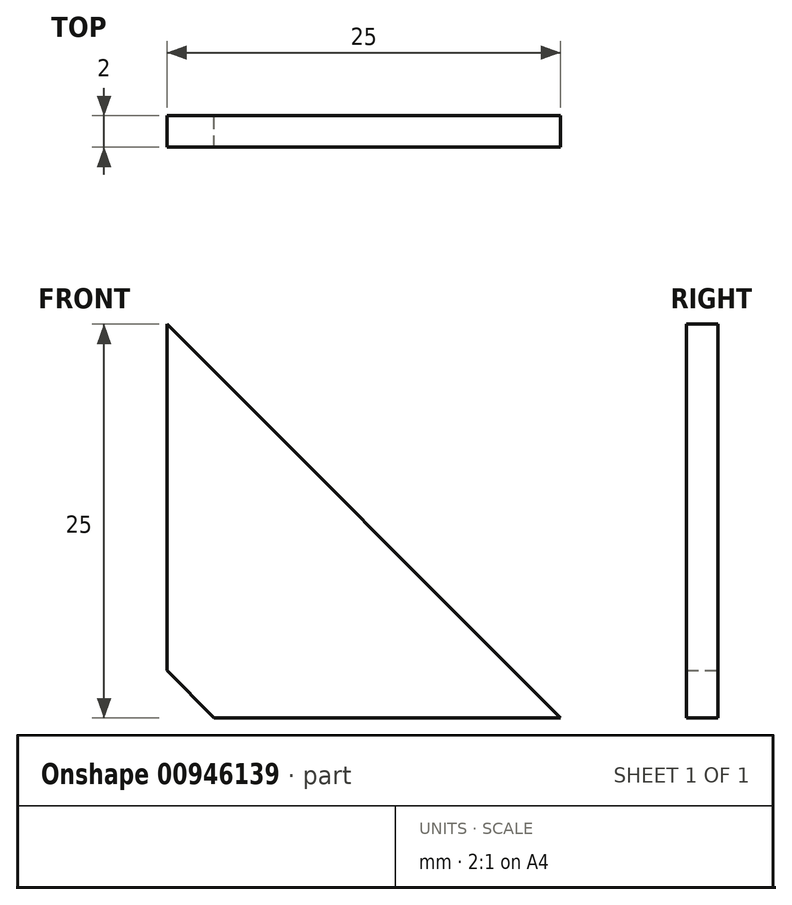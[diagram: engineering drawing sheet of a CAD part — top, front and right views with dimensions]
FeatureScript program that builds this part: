
annotation { "Feature Type Name" : "Feature", "Feature Type Description" : "" }
export const myFeature = defineFeature(function(context is Context, id is Id, definition is map)
    precondition{}
    {
        {
            var Q0;
            Q0=qCreatedBy(makeId("Front.planeOp"),FACE);
            var sketch = newSketch(context, id + "F0", { "sketchPlane" : qUnion([Q0])});
            skLineSegment(sketch, "E0", {"start": v(0, 0) * mm, "end": v(0, 25) * mm});
            skLineSegment(sketch, "E1", {"start": v(0, 25) * mm, "end": v(25, 0) * mm});
            skLineSegment(sketch, "E2", {"start": v(25, 0) * mm, "end": v(0, 0) * mm});
            skLineSegment(sketch, "E3", {"start": v(0, 3) * mm, "end": v(3, 0) * mm});
            skSolve(sketch);
        }
        {
            var Q0;
            {var subQ0=sQuery(id+"F0.wireOp",EDGE,"E1");Q0=makeQuery(id+"F0.imprint","IMPRINT",FACE,{"disambiguationData":[TD([[makeQuery(id+"F0.imprint","IMPRINT",EDGE,{"derivedFrom":subQ0}),-1.0]])]});}
            extrude(context, id + "F1", {"entities" : qUnion([Q0]), "depth" : 2 * mm, "offsetDistance" : 25 * mm});
        }
    });
